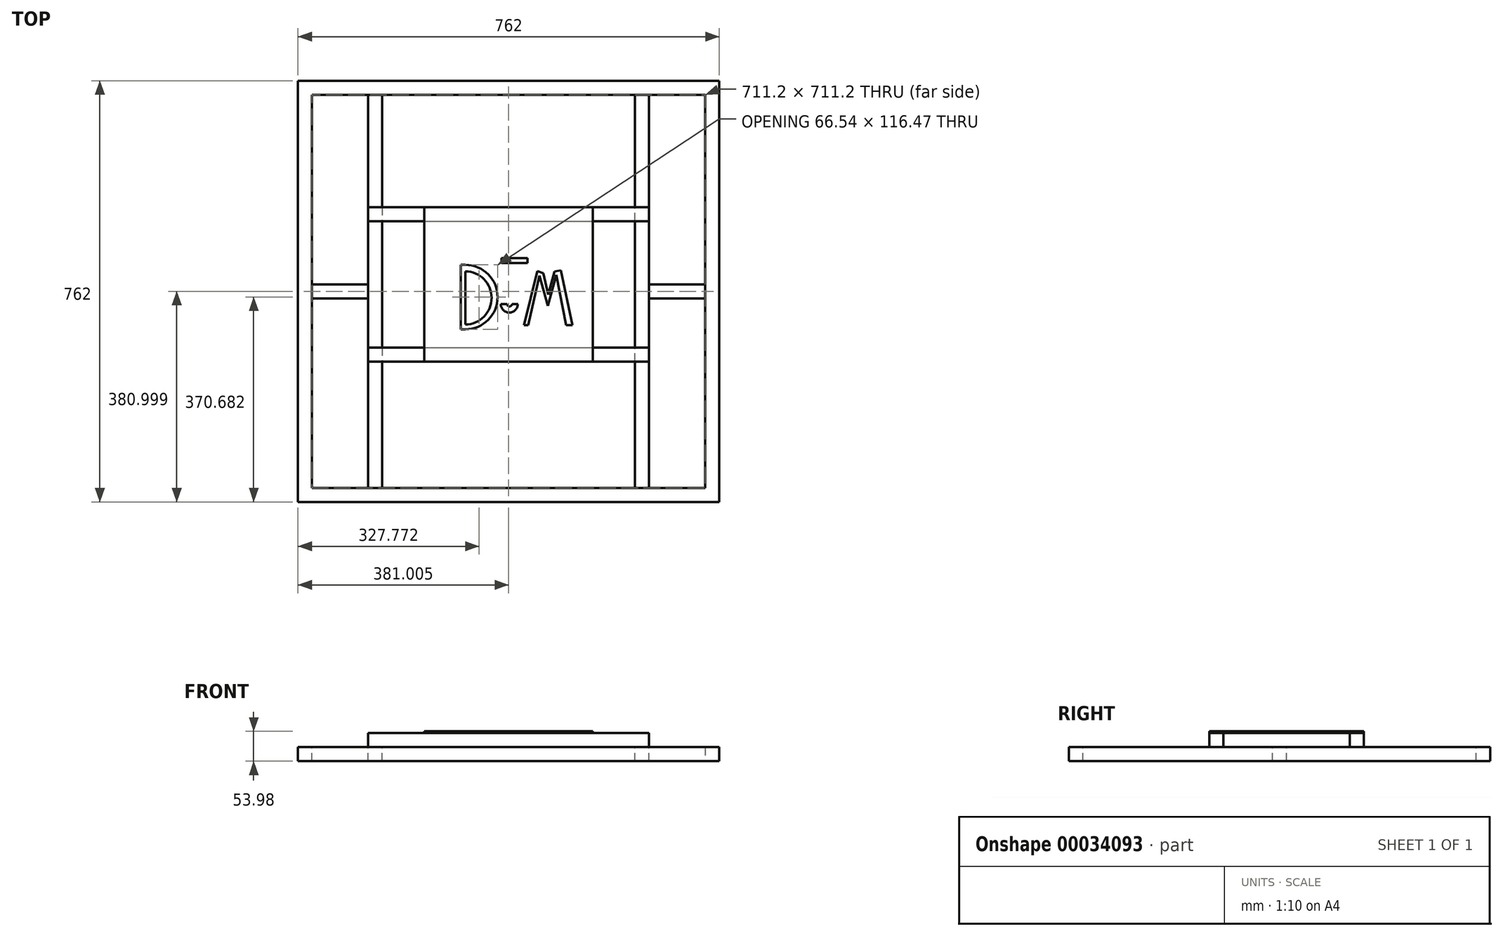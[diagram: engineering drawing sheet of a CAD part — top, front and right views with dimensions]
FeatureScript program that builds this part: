
annotation { "Feature Type Name" : "Feature", "Feature Type Description" : "" }
export const myFeature = defineFeature(function(context is Context, id is Id, definition is map)
    precondition{}
    {
        {
            var Q0;
            Q0=qCreatedBy(makeId("Top.planeOp"),FACE);
            var sketch = newSketch(context, id + "F0", { "sketchPlane" : qUnion([Q0])});
            skLineSegment(sketch, "E0.bottom", {"start": v(-350.06, 497.4) * mm, "end": v(411.94, 497.4) * mm});
            skLineSegment(sketch, "E0.top", {"start": v(-350.06, -264.6) * mm, "end": v(411.94, -264.6) * mm});
            skLineSegment(sketch, "E0.left", {"start": v(-350.06, 497.4) * mm, "end": v(-350.06, -264.6) * mm});
            skLineSegment(sketch, "E0.right", {"start": v(411.94, 497.4) * mm, "end": v(411.94, -264.6) * mm});
            skLineSegment(sketch, "E1.bottom", {"start": v(-324.66, 472) * mm, "end": v(386.54, 472) * mm});
            skLineSegment(sketch, "E1.top", {"start": v(-324.66, -239.2) * mm, "end": v(386.54, -239.2) * mm});
            skLineSegment(sketch, "E1.left", {"start": v(-324.66, 472) * mm, "end": v(-324.66, -239.2) * mm});
            skLineSegment(sketch, "E1.right", {"start": v(386.54, 472) * mm, "end": v(386.54, -239.2) * mm});
            skSolve(sketch);
        }
        {
            var Q0;
            Q0=makeQuery(id+"F0.imprint","IMPRINT",FACE,{"disambiguationData":[TD([[makeQuery(id+"F0.imprint","IMPRINT",EDGE,{"derivedFrom":sQuery(id+"F0.wireOp",EDGE,"E0.bottom")}),-1.0]])]});
            extrude(context, id + "F1", {"entities" : qUnion([Q0]), "depth" : 25.4 * mm});
        }
        {
            var Q0;
            Q0=makeQuery(id+"F1.opExtrude","CAP_FACE",FACE,{"disambiguationData":[OSD([sQuery(id+"F0.wireOp",EDGE,"E0.bottom"),sQuery(id+"F0.wireOp",EDGE,"E0.top"),sQuery(id+"F0.wireOp",EDGE,"E0.left"),sQuery(id+"F0.wireOp",EDGE,"E0.right"),sQuery(id+"F0.wireOp",EDGE,"E1.bottom"),sQuery(id+"F0.wireOp",EDGE,"E1.top"),sQuery(id+"F0.wireOp",EDGE,"E1.left"),sQuery(id+"F0.wireOp",EDGE,"E1.right")])],"isStart":false});
            var sketch = newSketch(context, id + "F2", { "sketchPlane" : qUnion([Q0])});
            skLineSegment(sketch, "E2.bottom", {"start": v(-223.06, 497.4) * mm, "end": v(-197.66, 497.4) * mm});
            skLineSegment(sketch, "E2.top", {"start": v(-223.06, -264.6) * mm, "end": v(-197.66, -264.6) * mm});
            skLineSegment(sketch, "E2.left", {"start": v(-223.06, 497.4) * mm, "end": v(-223.06, -264.6) * mm});
            skLineSegment(sketch, "E2.right", {"start": v(-197.66, 497.4) * mm, "end": v(-197.66, -264.6) * mm});
            skLineSegment(sketch, "E3.bottom", {"start": v(284.94, -264.6) * mm, "end": v(259.54, -264.6) * mm});
            skLineSegment(sketch, "E3.top", {"start": v(284.94, 497.4) * mm, "end": v(259.54, 497.4) * mm});
            skLineSegment(sketch, "E3.left", {"start": v(284.94, -264.6) * mm, "end": v(284.94, 497.4) * mm});
            skLineSegment(sketch, "E3.right", {"start": v(259.54, -264.6) * mm, "end": v(259.54, 497.4) * mm});
            skSolve(sketch);
        }
        {
            var Q0;
            {var subQ0=makeQuery(id+"F1.opExtrude","CAP_EDGE",EDGE,{"disambiguationData":[OSD([sQuery(id+"F0.wireOp",EDGE,"E1.top")])],"isStart":false});var subQ3=sQuery(id+"F2.wireOp",EDGE,"E3.left");var subQ4=makeQuery(id+"F2.imprint","INTERSECT",VERTEX,{"derivedFrom":[subQ0,subQ3]});Q0=makeQuery(id+"F2.imprint","IMPRINT",FACE,{"disambiguationData":[TD([[makeQuery(id+"F2.imprint","IMPRINT",EDGE,{"disambiguationData":[TD([[subQ4,-1.0]])],"derivedFrom":subQ3}),1.0]])]});}
            var Q1;
            {var subQ3=sQuery(id+"F2.wireOp",EDGE,"E2.left");var subQ5=makeQuery(id+"F1.opExtrude","CAP_EDGE",EDGE,{"disambiguationData":[OSD([sQuery(id+"F0.wireOp",EDGE,"E1.bottom")])],"isStart":false});var subQ7=makeQuery(id+"F2.imprint","INTERSECT",VERTEX,{"derivedFrom":[subQ5,subQ3]});Q1=makeQuery(id+"F2.imprint","IMPRINT",FACE,{"disambiguationData":[TD([[makeQuery(id+"F2.imprint","IMPRINT",EDGE,{"disambiguationData":[TD([[subQ7,-1.0]])],"derivedFrom":subQ3}),1.0]])]});}
            extrude(context, id + "F3", {"entities" : qUnion([Q0, Q1]), "oppositeDirection" : true, "depth" : 25.4 * mm});
        }
        {
            var Q0;
            Q0=makeQuery(id+"F3.opExtrude","CAP_FACE",FACE,{"disambiguationData":[OSD([sQuery(id+"F0.wireOp",EDGE,"E1.bottom"),sQuery(id+"F0.wireOp",EDGE,"E1.top"),sQuery(id+"F2.wireOp",EDGE,"E2.left"),sQuery(id+"F2.wireOp",EDGE,"E2.right")])],"isStart":true});
            var sketch = newSketch(context, id + "F4", { "sketchPlane" : qUnion([Q0])});
            skLineSegment(sketch, "E4.bottom", {"start": v(-223.06, 14.8) * mm, "end": v(284.94, 14.8) * mm});
            skLineSegment(sketch, "E4.top", {"start": v(-223.06, -10.6) * mm, "end": v(284.94, -10.6) * mm});
            skLineSegment(sketch, "E4.left", {"start": v(-223.06, -10.6) * mm, "end": v(-223.06, 14.8) * mm});
            skLineSegment(sketch, "E4.right", {"start": v(284.94, -10.6) * mm, "end": v(284.94, 14.8) * mm});
            skLineSegment(sketch, "E5.bottom", {"start": v(-223.06, 243.4) * mm, "end": v(284.94, 243.4) * mm});
            skLineSegment(sketch, "E5.top", {"start": v(-223.06, 268.8) * mm, "end": v(284.94, 268.8) * mm});
            skLineSegment(sketch, "E5.left", {"start": v(-223.06, 268.8) * mm, "end": v(-223.06, 243.4) * mm});
            skLineSegment(sketch, "E5.right", {"start": v(284.94, 268.8) * mm, "end": v(284.94, 243.4) * mm});
            skLineSegment(sketch, "E6.bottom", {"start": v(-197.66, 103.7) * mm, "end": v(-324.66, 103.7) * mm});
            skLineSegment(sketch, "E6.top", {"start": v(-197.66, 129.1) * mm, "end": v(-324.66, 129.1) * mm});
            skLineSegment(sketch, "E6.left", {"start": v(-197.66, 103.7) * mm, "end": v(-197.66, 129.1) * mm});
            skLineSegment(sketch, "E6.right", {"start": v(-324.66, 103.7) * mm, "end": v(-324.66, 129.1) * mm});
            skLineSegment(sketch, "E7.bottom", {"start": v(284.94, 243.4) * mm, "end": v(284.94, 243.4) * mm});
            skLineSegment(sketch, "E7.top", {"start": v(284.94, 14.8) * mm, "end": v(284.94, 14.8) * mm});
            skLineSegment(sketch, "E7.left", {"start": v(284.94, 243.4) * mm, "end": v(284.94, 14.8) * mm});
            skLineSegment(sketch, "E7.right", {"start": v(284.94, 243.4) * mm, "end": v(284.94, 14.8) * mm});
            skLineSegment(sketch, "E8.bottom", {"start": v(284.94, 129.1) * mm, "end": v(411.94, 129.1) * mm});
            skLineSegment(sketch, "E8.top", {"start": v(284.94, 103.7) * mm, "end": v(411.94, 103.7) * mm});
            skLineSegment(sketch, "E8.left", {"start": v(284.94, 129.1) * mm, "end": v(284.94, 103.7) * mm});
            skLineSegment(sketch, "E8.right", {"start": v(411.94, 129.1) * mm, "end": v(411.94, 103.7) * mm});
            skSolve(sketch);
        }
        {
            var Q0;
            {var subQ5=sQuery(id+"F4.wireOp",EDGE,"E4.right");Q0=makeQuery(id+"F4.imprint","IMPRINT",FACE,{"disambiguationData":[TD([[makeQuery(id+"F4.imprint","IMPRINT",EDGE,{"derivedFrom":subQ5}),1.0]])]});}
            var Q1;
            {var subQ0=sQuery(id+"F4.wireOp",EDGE,"E5.right");Q1=makeQuery(id+"F4.imprint","IMPRINT",FACE,{"disambiguationData":[TD([[makeQuery(id+"F4.imprint","IMPRINT",EDGE,{"derivedFrom":subQ0}),-1.0]])]});}
            var Q2;
            {var subQ0=sQuery(id+"F4.wireOp",EDGE,"E4.left");Q2=makeQuery(id+"F4.imprint","IMPRINT",FACE,{"disambiguationData":[TD([[makeQuery(id+"F4.imprint","IMPRINT",EDGE,{"derivedFrom":subQ0}),1.0]])]});}
            var Q3;
            {var subQ5=sQuery(id+"F4.wireOp",EDGE,"E5.left");Q3=makeQuery(id+"F4.imprint","IMPRINT",FACE,{"disambiguationData":[TD([[makeQuery(id+"F4.imprint","IMPRINT",EDGE,{"derivedFrom":subQ5}),1.0]])]});}
            extrude(context, id + "F5", {"entities" : qUnion([Q0, Q1, Q2, Q3]), "depth" : 25.4 * mm});
        }
        {
            var Q0;
            Q0=makeQuery(id+"F1.opExtrude","CAP_FACE",FACE,{"disambiguationData":[OSD([sQuery(id+"F0.wireOp",EDGE,"E0.bottom"),sQuery(id+"F0.wireOp",EDGE,"E0.top"),sQuery(id+"F0.wireOp",EDGE,"E0.left"),sQuery(id+"F0.wireOp",EDGE,"E0.right"),sQuery(id+"F0.wireOp",EDGE,"E1.bottom"),sQuery(id+"F0.wireOp",EDGE,"E1.top"),sQuery(id+"F0.wireOp",EDGE,"E1.left"),sQuery(id+"F0.wireOp",EDGE,"E1.right")])],"isStart":false});
            var sketch = newSketch(context, id + "F6", { "sketchPlane" : qUnion([Q0])});
            skLineSegment(sketch, "E9.bottom", {"start": v(411.94, 103.7) * mm, "end": v(284.94, 103.7) * mm});
            skLineSegment(sketch, "E9.top", {"start": v(411.94, 129.1) * mm, "end": v(284.94, 129.1) * mm});
            skLineSegment(sketch, "E9.left", {"start": v(411.94, 103.7) * mm, "end": v(411.94, 129.1) * mm});
            skLineSegment(sketch, "E9.right", {"start": v(284.94, 103.7) * mm, "end": v(284.94, 129.1) * mm});
            skLineSegment(sketch, "E10.bottom", {"start": v(-350.06, 103.7) * mm, "end": v(-223.06, 103.7) * mm});
            skLineSegment(sketch, "E10.top", {"start": v(-350.06, 129.1) * mm, "end": v(-223.06, 129.1) * mm});
            skLineSegment(sketch, "E10.left", {"start": v(-350.06, 103.7) * mm, "end": v(-350.06, 129.1) * mm});
            skLineSegment(sketch, "E10.right", {"start": v(-223.06, 103.7) * mm, "end": v(-223.06, 129.1) * mm});
            skSolve(sketch);
        }
        {
            var Q0;
            {var subQ5=sQuery(id+"F6.wireOp",EDGE,"E9.right");Q0=makeQuery(id+"F6.imprint","IMPRINT",FACE,{"disambiguationData":[TD([[makeQuery(id+"F6.imprint","IMPRINT",EDGE,{"derivedFrom":subQ5}),-1.0]])]});}
            var Q1;
            {var subQ5=sQuery(id+"F6.wireOp",EDGE,"E10.right");Q1=makeQuery(id+"F6.imprint","IMPRINT",FACE,{"disambiguationData":[TD([[makeQuery(id+"F6.imprint","IMPRINT",EDGE,{"derivedFrom":subQ5}),1.0]])]});}
            extrude(context, id + "F7", {"entities" : qUnion([Q0, Q1]), "oppositeDirection" : true, "depth" : 25.4 * mm});
        }
        {
            var Q0;
            Q0=makeQuery(id+"F5.opExtrude","CAP_FACE",FACE,{"disambiguationData":[OSD([sQuery(id+"F4.wireOp",EDGE,"E4.bottom"),sQuery(id+"F4.wireOp",EDGE,"E4.top"),sQuery(id+"F4.wireOp",EDGE,"E4.left"),sQuery(id+"F4.wireOp",EDGE,"E4.right")])],"isStart":false});
            var sketch = newSketch(context, id + "F8", { "sketchPlane" : qUnion([Q0])});
            skLineSegment(sketch, "E11.bottom", {"start": v(183.34, -10.6) * mm, "end": v(-121.46, -10.6) * mm});
            skLineSegment(sketch, "E11.top", {"start": v(183.34, 268.8) * mm, "end": v(-121.46, 268.8) * mm});
            skLineSegment(sketch, "E11.left", {"start": v(183.34, -10.6) * mm, "end": v(183.34, 268.8) * mm});
            skLineSegment(sketch, "E11.right", {"start": v(-121.46, -10.6) * mm, "end": v(-121.46, 268.8) * mm});
            skSolve(sketch);
        }
        {
            var Q0;
            {var subQ6=sQuery(id+"F8.wireOp",EDGE,"E11.bottom");Q0=makeQuery(id+"F8.imprint","IMPRINT",FACE,{"disambiguationData":[TD([[makeQuery(id+"F8.imprint","IMPRINT",EDGE,{"derivedFrom":subQ6}),1.0]])]});}
            var Q1;
            {var subQ5=sQuery(id+"F8.wireOp",EDGE,"E11.top");Q1=makeQuery(id+"F8.imprint","IMPRINT",FACE,{"disambiguationData":[TD([[makeQuery(id+"F8.imprint","IMPRINT",EDGE,{"derivedFrom":subQ5}),1.0]])]});}
            extrude(context, id + "F9", {"entities" : qUnion([Q0, Q1]), "depth" : 3.17 * mm});
        }
        {
            var Q0;
            Q0=makeQuery(id+"F9.opExtrude","CAP_FACE",FACE,{"disambiguationData":[OSD([sQuery(id+"F8.wireOp",EDGE,"E11.bottom"),sQuery(id+"F8.wireOp",EDGE,"E11.top"),sQuery(id+"F8.wireOp",EDGE,"E11.left"),sQuery(id+"F8.wireOp",EDGE,"E11.right")])],"isStart":false});
            var sketch = newSketch(context, id + "F10", { "sketchPlane" : qUnion([Q0])});
            skLineSegment(sketch, "E12.bottom", {"start": v(-55.56, 164.33) * mm, "end": v(-47.26, 164.33) * mm});
            skLineSegment(sketch, "E12.top", {"start": v(-55.56, 47.86) * mm, "end": v(-47.26, 47.86) * mm});
            skLineSegment(sketch, "E12.left", {"start": v(-55.56, 164.33) * mm, "end": v(-55.56, 47.86) * mm});
            skLineSegment(sketch, "E12.right", {"start": v(-47.26, 164.33) * mm, "end": v(-47.26, 47.86) * mm});
            skArc(sketch, "E13", {"start": v(-47.26, 47.86) * mm, "mid": v(10.98, 106.1) * mm, "end": v(-47.26, 164.33) * mm});
            skArc(sketch, "E14", {"start": v(-47.26, 56.4) * mm, "mid": v(0.05, 104.6) * mm, "end": v(-47.26, 152.8) * mm});
            skLineSegment(sketch, "E15.bottom", {"start": v(17.78, 176.68) * mm, "end": v(65.08, 176.68) * mm});
            skLineSegment(sketch, "E15.top", {"start": v(17.78, 167.43) * mm, "end": v(65.08, 167.43) * mm});
            skLineSegment(sketch, "E15.left", {"start": v(17.78, 176.68) * mm, "end": v(17.78, 167.43) * mm});
            skLineSegment(sketch, "E15.right", {"start": v(65.08, 176.68) * mm, "end": v(65.08, 167.43) * mm});
            skLineSegment(sketch, "E16.bottom", {"start": v(36.94, 167.43) * mm, "end": v(47.63, 167.43) * mm});
            skLineSegment(sketch, "E16.top", {"start": v(36.94, 93.66) * mm, "end": v(47.63, 93.66) * mm});
            skLineSegment(sketch, "E16.left", {"start": v(36.94, 167.43) * mm, "end": v(36.94, 93.66) * mm});
            skLineSegment(sketch, "E16.right", {"start": v(47.63, 167.43) * mm, "end": v(47.63, 93.66) * mm});
            skArc(sketch, "E17", {"start": v(16.59, 93.66) * mm, "mid": v(32.1, 78.14) * mm, "end": v(47.63, 93.66) * mm});
            skArc(sketch, "E18", {"start": v(27.98, 93.66) * mm, "mid": v(32.46, 89.18) * mm, "end": v(36.94, 93.66) * mm});
            skLineSegment(sketch, "E19", {"start": v(27.98, 93.66) * mm, "end": v(16.59, 93.66) * mm});
            skLineSegment(sketch, "E20", {"start": v(66.59, 55.6) * mm, "end": v(86.98, 144.98) * mm});
            skLineSegment(sketch, "E21", {"start": v(86.98, 144.98) * mm, "end": v(101.95, 90.4) * mm});
            skLineSegment(sketch, "E22", {"start": v(101.95, 90.4) * mm, "end": v(117.2, 146.42) * mm});
            skLineSegment(sketch, "E23", {"start": v(117.2, 146.42) * mm, "end": v(134.72, 55.1) * mm});
            skLineSegment(sketch, "E24", {"start": v(134.72, 55.1) * mm, "end": v(146.05, 55.1) * mm});
            skLineSegment(sketch, "E25", {"start": v(146.05, 55.1) * mm, "end": v(125.23, 154.56) * mm});
            skLineSegment(sketch, "E26", {"start": v(125.23, 154.56) * mm, "end": v(113.85, 152.18) * mm});
            skLineSegment(sketch, "E27", {"start": v(113.85, 152.18) * mm, "end": v(102.46, 110.37) * mm});
            skLineSegment(sketch, "E28", {"start": v(102.46, 110.37) * mm, "end": v(93.56, 149.02) * mm});
            skLineSegment(sketch, "E29", {"start": v(93.56, 149.02) * mm, "end": v(83.1, 153.18) * mm});
            skLineSegment(sketch, "E30", {"start": v(83.1, 153.18) * mm, "end": v(58.62, 55.22) * mm});
            skLineSegment(sketch, "E31", {"start": v(58.62, 55.22) * mm, "end": v(66.59, 55.6) * mm});
            skSolve(sketch);
        }
        {
            var Q0;
            {var subQ4=sQuery(id+"F10.wireOp",EDGE,"E12.bottom");Q0=makeQuery(id+"F10.imprint","IMPRINT",FACE,{"disambiguationData":[TD([[makeQuery(id+"F10.imprint","IMPRINT",EDGE,{"derivedFrom":subQ4}),-1.0]])]});}
            var Q1;
            {var subQ1=sQuery(id+"F10.wireOp",EDGE,"E13");Q1=makeQuery(id+"F10.imprint","IMPRINT",FACE,{"disambiguationData":[TD([[makeQuery(id+"F10.imprint","IMPRINT",EDGE,{"derivedFrom":subQ1}),1.0]])]});}
            var Q2;
            Q2=makeQuery(id+"F10.imprint","IMPRINT",FACE,{"disambiguationData":[TD([[makeQuery(id+"F10.imprint","IMPRINT",EDGE,{"derivedFrom":sQuery(id+"F10.wireOp",EDGE,"E16.bottom")}),-1.0]])]});
            var Q3;
            Q3=makeQuery(id+"F10.imprint","IMPRINT",FACE,{"disambiguationData":[TD([[makeQuery(id+"F10.imprint","IMPRINT",EDGE,{"derivedFrom":sQuery(id+"F10.wireOp",EDGE,"E15.bottom")}),-1.0]])]});
            var Q4;
            Q4=makeQuery(id+"F10.imprint","IMPRINT",FACE,{"disambiguationData":[TD([[makeQuery(id+"F10.imprint","IMPRINT",EDGE,{"derivedFrom":sQuery(id+"F10.wireOp",EDGE,"E16.top")}),-1.0]])]});
            var Q5;
            Q5=makeQuery(id+"F10.imprint","IMPRINT",FACE,{"disambiguationData":[TD([[makeQuery(id+"F10.imprint","IMPRINT",EDGE,{"derivedFrom":sQuery(id+"F10.wireOp",EDGE,"E20")}),1.0]])]});
            extrude(context, id + "F11", {"entities" : qUnion([Q0, Q1, Q2, Q3, Q4, Q5]), "operationType" : NewBodyOperationType.REMOVE, "endBound" : BoundingType.SYMMETRIC, "oppositeDirection" : true, "depth" : 25.4 * mm});
        }
    });
